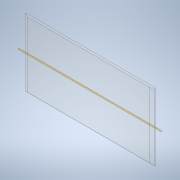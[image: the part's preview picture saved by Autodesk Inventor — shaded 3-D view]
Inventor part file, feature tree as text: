
AUTODESK INVENTOR PART (.ipt)
format: ipt  version: 2020 (Build 240168000, 168)  size: 136,192 bytes
history: native  units: in
note: dims shown in document units (in); Inventor stores cm internally (conversion verified against a paired STEP export)
features: extrude x4, sketch x4, projected_geometry x3, plane x1
ambient origin geometry x8: Origin, YZ Plane, XZ Plane, XY Plane, X Axis, Y Axis, Z Axis, Center Point
bodies: Solid1 (feature_tree)
feature tree (12):
  extrude  "Extrusion1"  Depth=12.515in
  extrude  "Extrusion2"  Depth=0.227in
  extrude  "Extrusion3"  TaperAngle=0.0deg  [1 undecoded]
  plane  "Work Plane1"
  extrude  "Extrusion4"  TaperAngle=135.0deg  [1 undecoded]
  sketch  "Sketch1"  dims[d0=24.0in d1=12.515in]
  sketch  "Sketch2"  dims[d2=0.227in d3=0.0in d4=0.1494in]
  projected_geometry  "Projected Loop1"
  sketch  "Sketch3"  dims[d5=90.0deg d6=0.0in d7=0.0in]
  projected_geometry  "Projected Loop2"
  sketch  "Sketch4"  dims[d8=135.0deg d9=135.0deg d10=0.0in d11=0.0in d12=6.2575in d13=1.0in d14=0.0205in d15=6.083in d16=0.0in]
  projected_geometry  "Projected Loop3"
note: 2 required parameter values undecoded (feature->parameter linkage not recoverable at this tier; creation-order binding heuristic only, values carry confidence <= 0.55)
